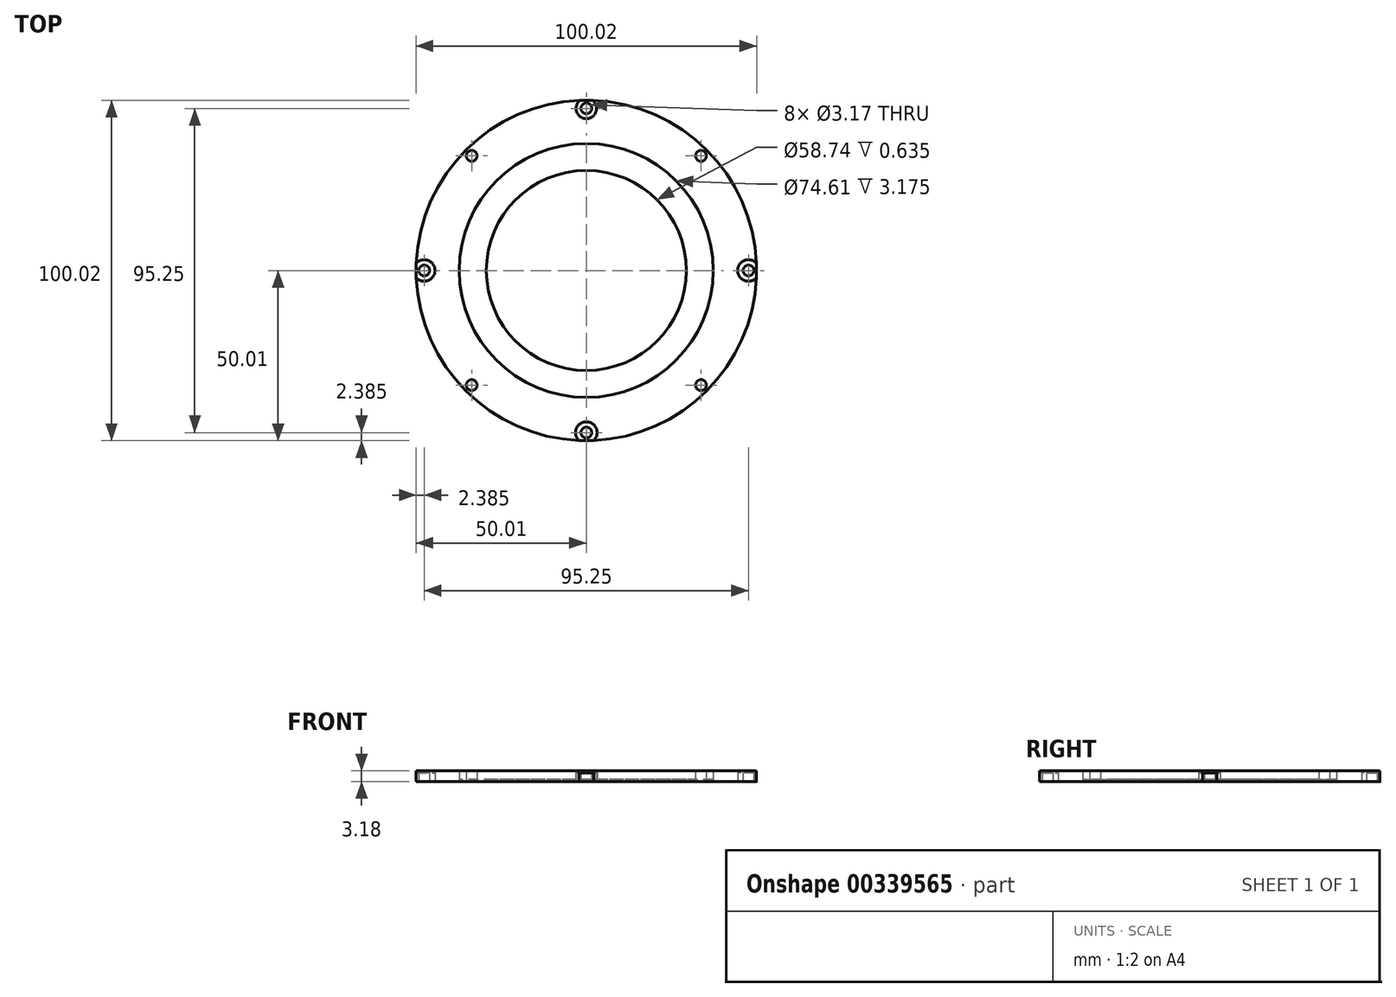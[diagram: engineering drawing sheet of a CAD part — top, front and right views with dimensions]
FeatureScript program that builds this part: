
annotation { "Feature Type Name" : "Feature", "Feature Type Description" : "" }
export const myFeature = defineFeature(function(context is Context, id is Id, definition is map)
    precondition{}
    {
        {
            var Q0;
            Q0=qCreatedBy(makeId("Top.planeOp"),FACE);
            var sketch = newSketch(context, id + "F0", { "sketchPlane" : qUnion([Q0])});
            skCircle(sketch, "E0", {"center": v(0, 0) * mm, "radius": 50 * mm});
            skCircle(sketch, "E1", {"center": v(0, 0) * mm, "radius": 37.3 * mm});
            skCircle(sketch, "E2", {"center": v(0, 0) * mm, "radius": 29.37 * mm});
            skCircle(sketch, "E3", {"center": v(0, 47.63) * mm, "radius": 1.59 * mm});
            skCircle(sketch, "E4.1.0", {"center": v(-33.68, 33.68) * mm, "radius": 1.59 * mm});
            skCircle(sketch, "E4.2.0", {"center": v(-47.63, 0) * mm, "radius": 1.59 * mm});
            skCircle(sketch, "E4.3.0", {"center": v(-33.68, -33.68) * mm, "radius": 1.59 * mm});
            skCircle(sketch, "E4.4.0", {"center": v(0, -47.63) * mm, "radius": 1.59 * mm});
            skCircle(sketch, "E4.5.0", {"center": v(33.68, -33.68) * mm, "radius": 1.59 * mm});
            skCircle(sketch, "E4.6.0", {"center": v(47.63, 0) * mm, "radius": 1.59 * mm});
            skCircle(sketch, "E4.7.0", {"center": v(33.68, 33.68) * mm, "radius": 1.59 * mm});
            skArc(sketch, "E5", {"start": v(-49.96, -2.15) * mm, "mid": v(-44.45, 0) * mm, "end": v(-49.96, 2.15) * mm});
            skArc(sketch, "E6", {"start": v(49.96, 2.15) * mm, "mid": v(44.45, 0) * mm, "end": v(49.96, -2.15) * mm});
            skArc(sketch, "E7", {"start": v(2.15, -49.96) * mm, "mid": v(0, -44.45) * mm, "end": v(-2.15, -49.96) * mm});
            skArc(sketch, "E8", {"start": v(-1.88, 49.97) * mm, "mid": v(0, 44.62) * mm, "end": v(1.88, 49.97) * mm});
            skSolve(sketch);
        }
        {
            var Q0;
            Q0=makeQuery(id+"F0.imprint","IMPRINT",FACE,{"disambiguationData":[TD([[makeQuery(id+"F0.imprint","IMPRINT",EDGE,{"derivedFrom":sQuery(id+"F0.wireOp",EDGE,"E3")}),-1.0]])]});
            var Q1;
            Q1=makeQuery(id+"F0.imprint","IMPRINT",FACE,{"disambiguationData":[TD([[makeQuery(id+"F0.imprint","IMPRINT",EDGE,{"derivedFrom":sQuery(id+"F0.wireOp",EDGE,"E4.2.0")}),-1.0]])]});
            var Q2;
            Q2=makeQuery(id+"F0.imprint","IMPRINT",FACE,{"disambiguationData":[TD([[makeQuery(id+"F0.imprint","IMPRINT",EDGE,{"derivedFrom":sQuery(id+"F0.wireOp",EDGE,"E4.4.0")}),-1.0]])]});
            var Q3;
            Q3=makeQuery(id+"F0.imprint","IMPRINT",FACE,{"disambiguationData":[TD([[makeQuery(id+"F0.imprint","IMPRINT",EDGE,{"derivedFrom":sQuery(id+"F0.wireOp",EDGE,"E4.6.0")}),-1.0]])]});
            extrude(context, id + "F1", {"entities" : qUnion([Q0, Q1, Q2, Q3]), "depth" : 2.54 * mm});
        }
        {
            var Q0;
            Q0=makeQuery(id+"F0.imprint","IMPRINT",FACE,{"disambiguationData":[TD([[makeQuery(id+"F0.imprint","IMPRINT",EDGE,{"derivedFrom":sQuery(id+"F0.wireOp",EDGE,"E1")}),1.0]])]});
            extrude(context, id + "F2", {"entities" : qUnion([Q0]), "depth" : 0.64 * mm});
        }
        {
            var Q0;
            Q0=makeQuery(id+"F0.imprint","IMPRINT",FACE,{"disambiguationData":[TD([[makeQuery(id+"F0.imprint","IMPRINT",EDGE,{"derivedFrom":sQuery(id+"F0.wireOp",EDGE,"E1")}),-1.0]])]});
            extrude(context, id + "F3", {"entities" : qUnion([Q0]), "depth" : 3.17 * mm});
        }
    });
